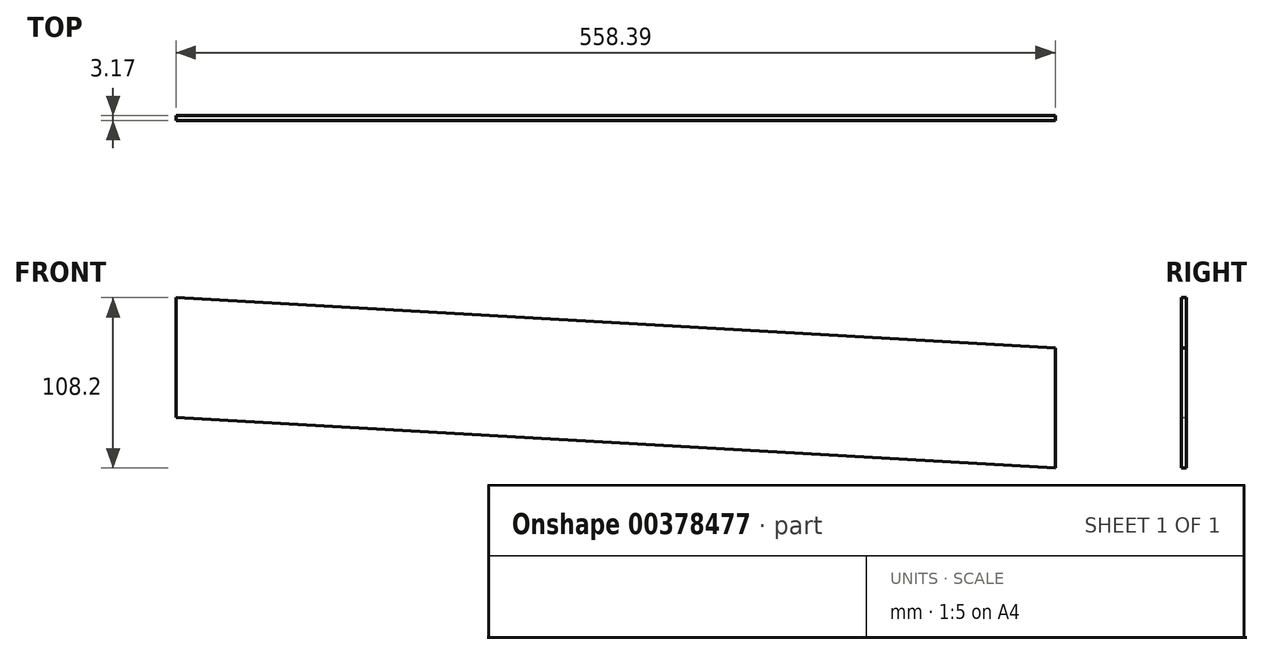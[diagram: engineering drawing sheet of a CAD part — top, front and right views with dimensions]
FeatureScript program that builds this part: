
annotation { "Feature Type Name" : "Feature", "Feature Type Description" : "" }
export const myFeature = defineFeature(function(context is Context, id is Id, definition is map)
    precondition{}
    {
        {
            var Q0;
            Q0=qCreatedBy(makeId("Front.planeOp"),FACE);
            var sketch = newSketch(context, id + "F0", { "sketchPlane" : qUnion([Q0])});
            skLineSegment(sketch, "E0", {"start": v(0, 0) * mm, "end": v(0, 76.2) * mm});
            skLineSegment(sketch, "E1", {"start": v(0, 76.2) * mm, "end": v(-558.4, 108.2) * mm});
            skLineSegment(sketch, "E2", {"start": v(-558.4, 108.2) * mm, "end": v(-558.4, 32) * mm});
            skLineSegment(sketch, "E3", {"start": v(-558.4, 32) * mm, "end": v(0, 0) * mm});
            skSolve(sketch);
        }
        {
            var Q0;
            Q0 = qSketchRegion(id + "F0", true);
            extrude(context, id + "F1", {"entities" : qUnion([Q0]), "depth" : 3.17 * mm});
        }
    });
